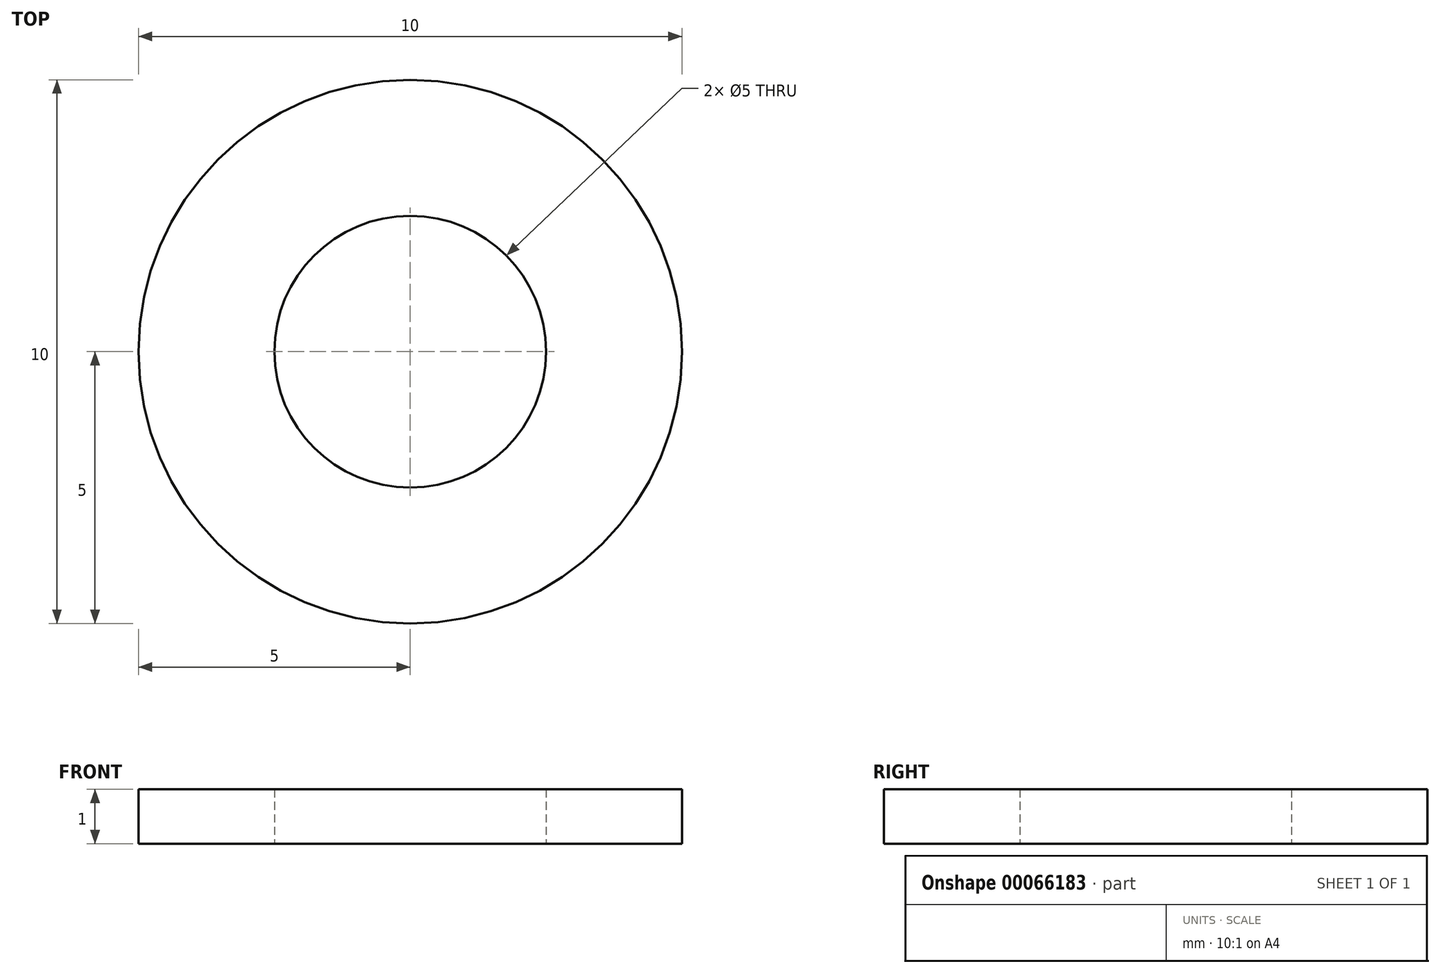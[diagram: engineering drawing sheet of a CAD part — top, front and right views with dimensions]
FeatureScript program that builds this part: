
annotation { "Feature Type Name" : "Feature", "Feature Type Description" : "" }
export const myFeature = defineFeature(function(context is Context, id is Id, definition is map)
    precondition{}
    {
        {
            var Q0;
            Q0=qCreatedBy(makeId("Top.planeOp"),FACE);
            var sketch = newSketch(context, id + "F0", { "sketchPlane" : qUnion([Q0])});
            skCircle(sketch, "E0", {"center": v(0, 0) * mm, "radius": 2.5 * mm});
            skCircle(sketch, "E1", {"center": v(0, 0) * mm, "radius": 5 * mm});
            skSolve(sketch);
        }
        {
            var Q0;
            Q0=makeQuery(id+"F0.imprint","IMPRINT",FACE,{"disambiguationData":[TD([[makeQuery(id+"F0.imprint","IMPRINT",EDGE,{"derivedFrom":sQuery(id+"F0.wireOp",EDGE,"E0")}),-1.0]])]});
            extrude(context, id + "F1", {"entities" : qUnion([Q0]), "depth" : 1 * mm, "offsetDistance" : 25 * mm});
        }
    });
